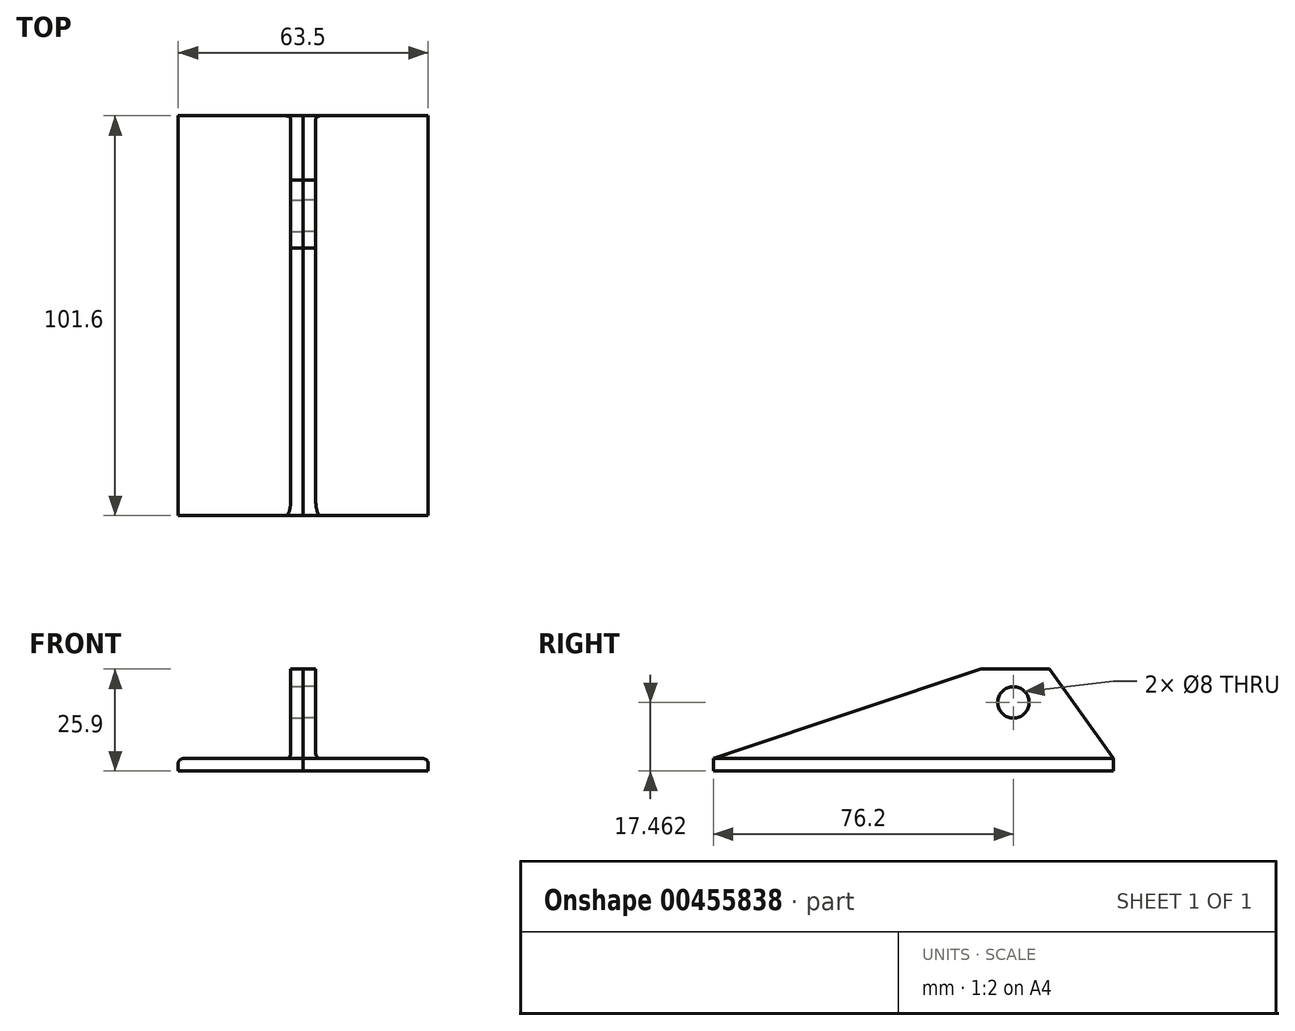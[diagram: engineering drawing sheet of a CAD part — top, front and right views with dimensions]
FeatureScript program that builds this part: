
annotation { "Feature Type Name" : "Feature", "Feature Type Description" : "" }
export const myFeature = defineFeature(function(context is Context, id is Id, definition is map)
    precondition{}
    {
        {
            var Q0;
            Q0=qCreatedBy(makeId("Front.planeOp"),FACE);
            var sketch = newSketch(context, id + "F0", { "sketchPlane" : qUnion([Q0])});
            skLineSegment(sketch, "E0", {"start": v(0, 0) * mm, "end": v(0, 31.75) * mm});
            skLineSegment(sketch, "E1", {"start": v(0, 31.75) * mm, "end": v(1.9, 31.75) * mm});
            skLineSegment(sketch, "E2", {"start": v(3.18, 30.48) * mm, "end": v(3.18, 4.44) * mm});
            skLineSegment(sketch, "E3", {"start": v(4.45, 3.17) * mm, "end": v(30.48, 3.17) * mm});
            skLineSegment(sketch, "E4", {"start": v(31.75, 1.9) * mm, "end": v(31.75, 0) * mm});
            skLineSegment(sketch, "E5", {"start": v(31.75, 0) * mm, "end": v(0, 0) * mm});
            skPoint(sketch, "E6.visualSharp", {"position": v(3.18, 3.17) * mm});
            skArc(sketch, "E6.filletArc", {"start": v(3.18, 4.44) * mm, "mid": v(3.55, 3.55) * mm, "end": v(4.45, 3.17) * mm});
            skPoint(sketch, "E7.visualSharp", {"position": v(31.75, 3.17) * mm});
            skArc(sketch, "E7.filletArc", {"start": v(31.75, 1.9) * mm, "mid": v(31.38, 2.8) * mm, "end": v(30.48, 3.17) * mm});
            skPoint(sketch, "E8.visualSharp", {"position": v(3.18, 31.75) * mm});
            skArc(sketch, "E8.filletArc", {"start": v(3.18, 30.48) * mm, "mid": v(2.8, 31.38) * mm, "end": v(1.9, 31.75) * mm});
            skSolve(sketch);
        }
        {
            var Q0;
            Q0 = qSketchRegion(id + "F0", true);
            extrude(context, id + "F1", {"entities" : qUnion([Q0]), "depth" : 101.6 * mm, "offsetDistance" : 25.4 * mm});
        }
        {
            var Q0;
            Q0=qCreatedBy(makeId("Right.planeOp"),FACE);
            var sketch = newSketch(context, id + "F2", { "sketchPlane" : qUnion([Q0])});
            skCircle(sketch, "E9", {"center": v(-25.4, 17.46) * mm, "radius": 4 * mm});
            skLineSegment(sketch, "E10", {"start": v(-33.65, 25.9) * mm, "end": v(-101.6, 3.17) * mm});
            skLineSegment(sketch, "E11", {"start": v(-101.6, 3.17) * mm, "end": v(-101.6, 31.75) * mm});
            skLineSegment(sketch, "E12", {"start": v(-101.6, 31.75) * mm, "end": v(0, 31.75) * mm});
            skLineSegment(sketch, "E13", {"start": v(0, 31.75) * mm, "end": v(0, 3.18) * mm});
            skLineSegment(sketch, "E14", {"start": v(0, 3.17) * mm, "end": v(-16.3, 25.9) * mm});
            skLineSegment(sketch, "E15", {"start": v(-16.3, 25.9) * mm, "end": v(-33.65, 25.9) * mm});
            skSolve(sketch);
        }
        {
            var Q0;
            Q0 = qSketchRegion(id + "F2", true);
            extrude(context, id + "F3", {"entities" : qUnion([Q0]), "operationType" : NewBodyOperationType.REMOVE, "endBound" : BoundingType.THROUGH_ALL, "depth" : 25.4 * mm, "offsetDistance" : 25.4 * mm});
        }
        {
            var Q0;
            Q0=makeQuery(id+"F1.opExtrude","SWEPT_BODY",BODY,{"disambiguationData":[OSD([sQuery(id+"F0.wireOp",EDGE,"E0"),sQuery(id+"F0.wireOp",EDGE,"E1"),sQuery(id+"F0.wireOp",EDGE,"E2"),sQuery(id+"F0.wireOp",EDGE,"E3"),sQuery(id+"F0.wireOp",EDGE,"E4"),sQuery(id+"F0.wireOp",EDGE,"E5"),sQuery(id+"F0.wireOp",EDGE,"E6.filletArc"),sQuery(id+"F0.wireOp",EDGE,"E7.filletArc"),sQuery(id+"F0.wireOp",EDGE,"E8.filletArc")])]});
            var Q1;
            Q1=qCreatedBy(makeId("Right.planeOp"),FACE);
            mirror(context, id + "F4", {"entities" : qUnion([Q0]), "mirrorPlane" : qUnion([Q1])});
        }
    });
